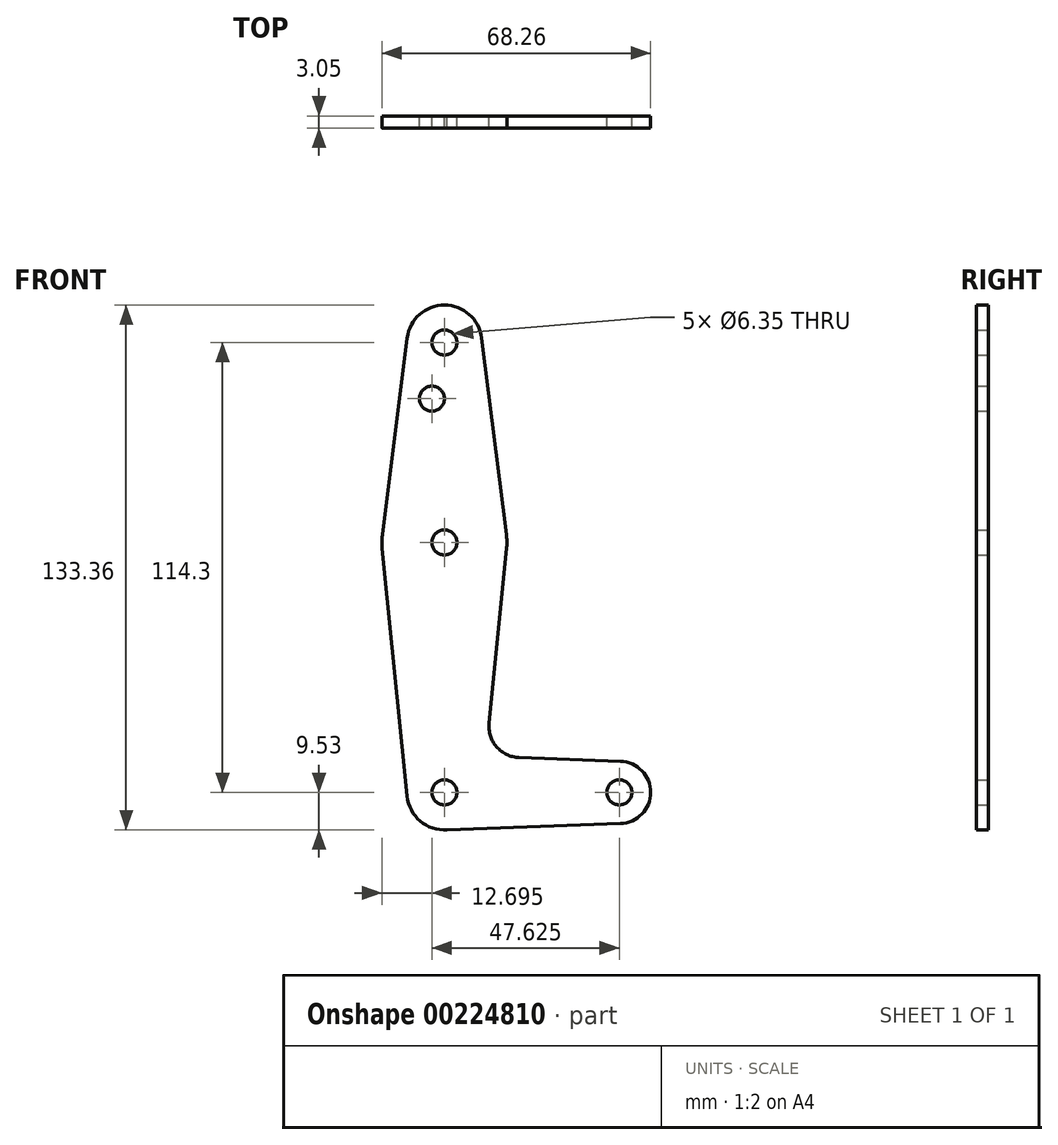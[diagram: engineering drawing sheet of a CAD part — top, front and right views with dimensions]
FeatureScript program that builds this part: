
annotation { "Feature Type Name" : "Feature", "Feature Type Description" : "" }
export const myFeature = defineFeature(function(context is Context, id is Id, definition is map)
    precondition{}
    {
        {
            var Q0;
            Q0=qCreatedBy(makeId("Front.planeOp"),FACE);
            var sketch = newSketch(context, id + "F0", { "sketchPlane" : qUnion([Q0])});
            skLineSegment(sketch, "E0", {"start": v(0, 114.3) * mm, "end": v(0, 0) * mm, "construction": true});
            skLineSegment(sketch, "E1", {"start": v(0, 0) * mm, "end": v(44.45, 0) * mm, "construction": true});
            skCircle(sketch, "E2", {"center": v(0, 114.3) * mm, "radius": 9.53 * mm});
            skCircle(sketch, "E3", {"center": v(0, 0) * mm, "radius": 9.53 * mm});
            skCircle(sketch, "E4", {"center": v(44.45, 0) * mm, "radius": 7.94 * mm});
            skCircle(sketch, "E5", {"center": v(0, 63.5) * mm, "radius": 15.88 * mm});
            skLineSegment(sketch, "E6", {"start": v(-9.45, 115.5) * mm, "end": v(-15.75, 65.48) * mm});
            skLineSegment(sketch, "E7", {"start": v(-15.8, 61.91) * mm, "end": v(-9.48, -0.95) * mm});
            skLineSegment(sketch, "E8", {"start": v(9.45, 115.5) * mm, "end": v(15.75, 65.48) * mm});
            skLineSegment(sketch, "E9", {"start": v(18.97, 8.85) * mm, "end": v(44.73, 7.93) * mm});
            skLineSegment(sketch, "E10", {"start": v(0, -9.53) * mm, "end": v(44.73, -7.93) * mm});
            skLineSegment(sketch, "E11", {"start": v(15.8, 61.91) * mm, "end": v(11.34, 17.6) * mm});
            skCircle(sketch, "E12", {"center": v(0, 114.3) * mm, "radius": 3.18 * mm});
            skCircle(sketch, "E13", {"center": v(0, 63.5) * mm, "radius": 3.18 * mm});
            skCircle(sketch, "E14", {"center": v(0, 0) * mm, "radius": 3.18 * mm});
            skCircle(sketch, "E15", {"center": v(44.45, 0) * mm, "radius": 3.18 * mm});
            skCircle(sketch, "E16", {"center": v(-3.18, 100.03) * mm, "radius": 3.18 * mm});
            skArc(sketch, "E17.filletArc", {"start": v(11.34, 17.6) * mm, "mid": v(13.26, 11.57) * mm, "end": v(18.97, 8.85) * mm});
            skSolve(sketch);
        }
        {
            var Q0;
            Q0 = qSketchRegion(id + "F0", true);
            extrude(context, id + "F1", {"entities" : qUnion([Q0]), "depth" : 3.05 * mm});
        }
    });
